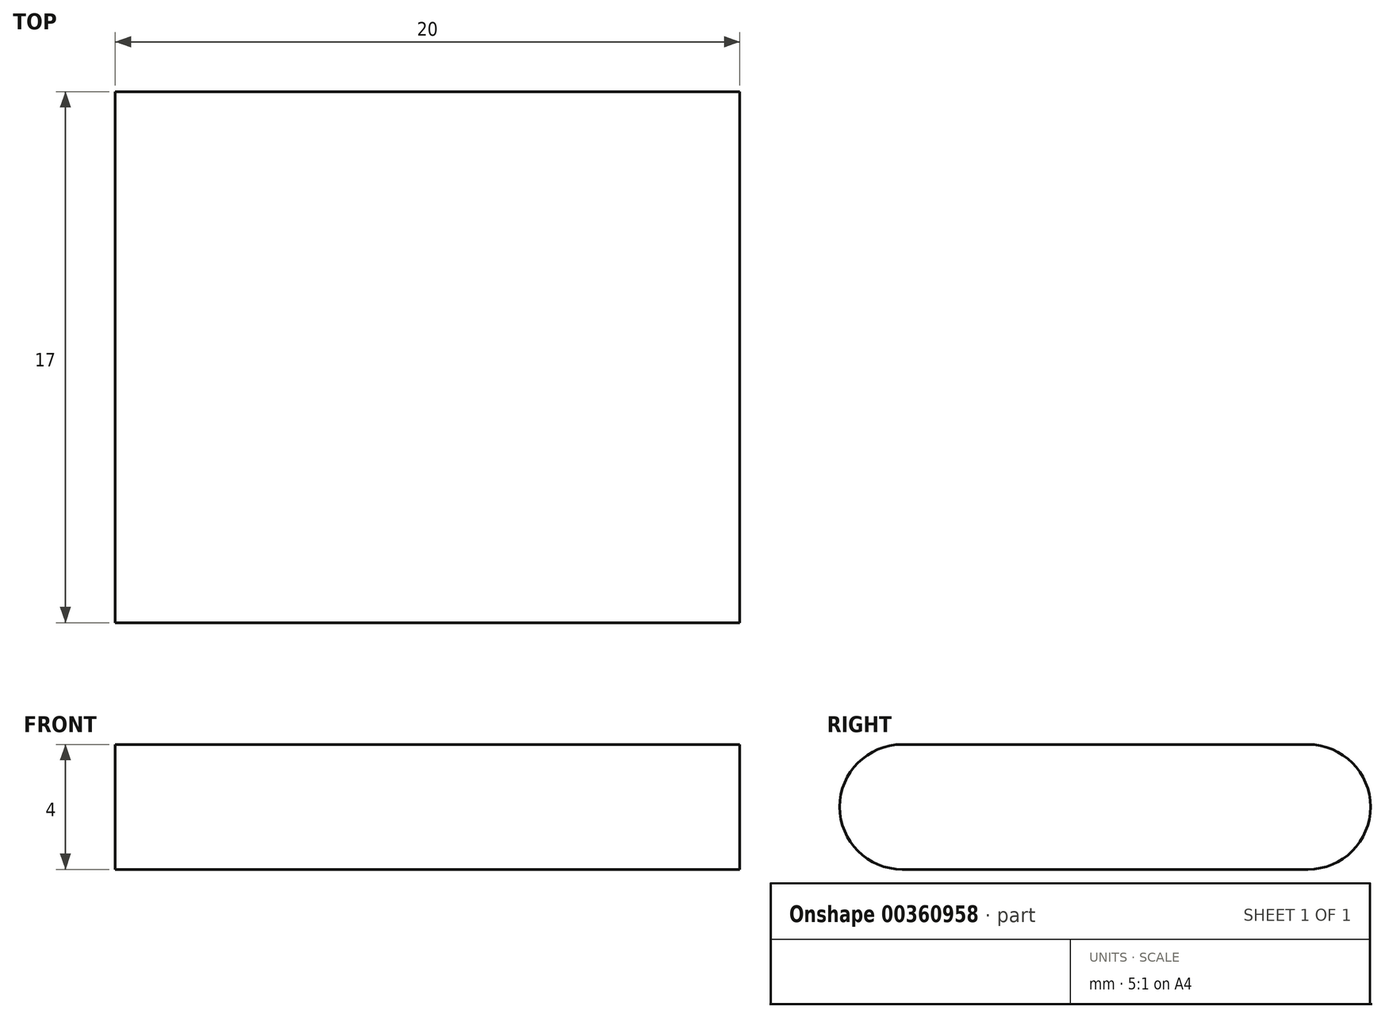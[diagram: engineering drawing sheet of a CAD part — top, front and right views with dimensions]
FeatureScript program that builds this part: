
annotation { "Feature Type Name" : "Feature", "Feature Type Description" : "" }
export const myFeature = defineFeature(function(context is Context, id is Id, definition is map)
    precondition{}
    {
        {
            var Q0;
            Q0=qCreatedBy(makeId("Right.planeOp"),FACE);
            var sketch = newSketch(context, id + "F0", { "sketchPlane" : qUnion([Q0])});
            skLineSegment(sketch, "E0", {"start": v(-6.5, 2) * mm, "end": v(6.5, 2) * mm});
            skArc(sketch, "E1", {"start": v(6.5, 2) * mm, "mid": v(8.5, 0) * mm, "end": v(6.5, -2) * mm});
            skLineSegment(sketch, "E2", {"start": v(6.5, -2) * mm, "end": v(-6.5, -2) * mm});
            skArc(sketch, "E3", {"start": v(-6.5, -2) * mm, "mid": v(-8.5, 0) * mm, "end": v(-6.5, 2) * mm});
            skSolve(sketch);
        }
        {
            var Q0;
            Q0=makeQuery(id+"F0.imprint","IMPRINT",FACE,{"disambiguationData":[TD([[makeQuery(id+"F0.imprint","IMPRINT",EDGE,{"derivedFrom":sQuery(id+"F0.wireOp",EDGE,"E0")}),-1.0]])]});
            extrude(context, id + "F1", {"entities" : qUnion([Q0]), "endBound" : BoundingType.SYMMETRIC, "depth" : 20 * mm});
        }
    });
